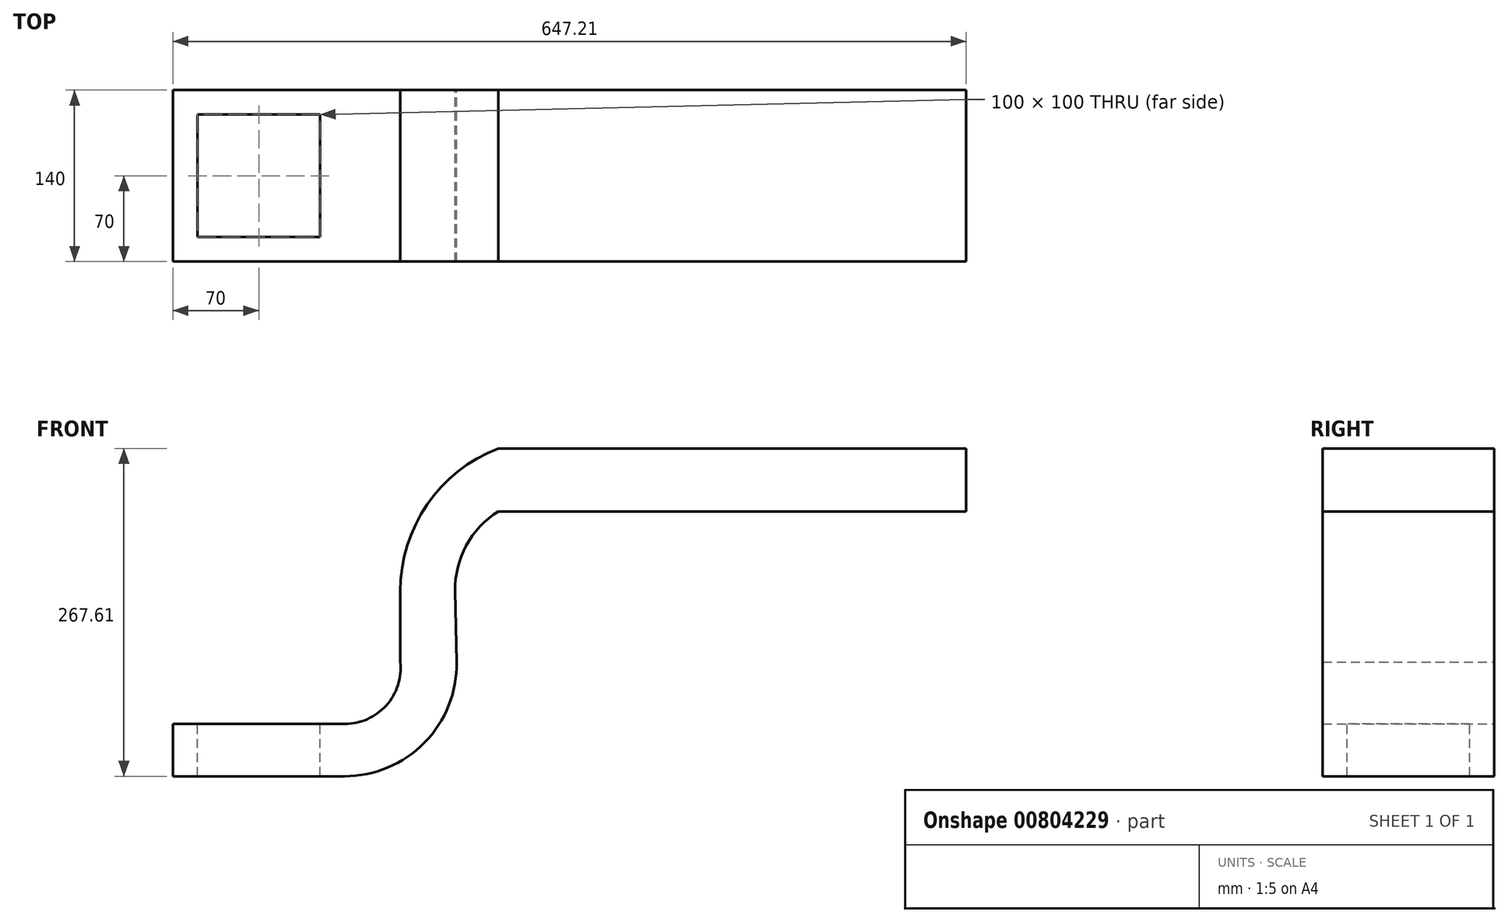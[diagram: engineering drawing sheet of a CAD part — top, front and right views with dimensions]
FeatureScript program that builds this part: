
annotation { "Feature Type Name" : "Feature", "Feature Type Description" : "" }
export const myFeature = defineFeature(function(context is Context, id is Id, definition is map)
    precondition{}
    {
        {
            var Q0;
            Q0=qCreatedBy(makeId("Front.planeOp"),FACE);
            var sketch = newSketch(context, id + "F0", { "sketchPlane" : qUnion([Q0])});
            skLineSegment(sketch, "E0", {"start": v(-140, 42.69) * mm, "end": v(-140, 0) * mm});
            skLineSegment(sketch, "E1", {"start": v(-140, 0) * mm, "end": v(0, 0) * mm});
            skArc(sketch, "E2", {"start": v(0, 0) * mm, "mid": v(65.24, 27.4) * mm, "end": v(91.34, 93.18) * mm});
            skLineSegment(sketch, "E3", {"start": v(-140, 42.69) * mm, "end": v(0, 42.69) * mm});
            skArc(sketch, "E4", {"start": v(0, 42.69) * mm, "mid": v(33.96, 57.82) * mm, "end": v(45.44, 93.18) * mm});
            skLineSegment(sketch, "E5", {"start": v(45.44, 93.18) * mm, "end": v(45.44, 151.02) * mm});
            skLineSegment(sketch, "E6", {"start": v(91.34, 93.18) * mm, "end": v(90.2, 150.92) * mm});
            skArc(sketch, "E7", {"start": v(125.31, 216.2) * mm, "mid": v(99.19, 188.17) * mm, "end": v(90.2, 150.92) * mm});
            skArc(sketch, "E8", {"start": v(125.31, 267.6) * mm, "mid": v(67.32, 221.68) * mm, "end": v(45.44, 151.02) * mm});
            skLineSegment(sketch, "E9", {"start": v(125.31, 216.2) * mm, "end": v(507.21, 216.2) * mm});
            skLineSegment(sketch, "E10", {"start": v(125.31, 267.6) * mm, "end": v(507.21, 267.6) * mm});
            skLineSegment(sketch, "E11", {"start": v(507.21, 267.6) * mm, "end": v(507.21, 216.2) * mm});
            skSolve(sketch);
        }
        {
            var Q0;
            Q0 = qSketchRegion(id + "F0", true);
            extrude(context, id + "F1", {"entities" : qUnion([Q0]), "depth" : 140 * mm, "offsetDistance" : 25.4 * mm});
        }
        {
            var Q0;
            Q0=makeQuery(id+"F1.opExtrude","SWEPT_FACE",FACE,{"disambiguationData":[OSD([sQuery(id+"F0.wireOp",EDGE,"E3")])]});
            var sketch = newSketch(context, id + "F2", { "sketchPlane" : qUnion([Q0])});
            skLineSegment(sketch, "E12.bottom", {"start": v(-20, -20) * mm, "end": v(-120, -20) * mm});
            skLineSegment(sketch, "E12.top", {"start": v(-20, -120) * mm, "end": v(-120, -120) * mm});
            skLineSegment(sketch, "E12.left", {"start": v(-20, -20) * mm, "end": v(-20, -120) * mm});
            skLineSegment(sketch, "E12.right", {"start": v(-120, -20) * mm, "end": v(-120, -120) * mm});
            skSolve(sketch);
        }
        {
            var Q0;
            Q0 = qSketchRegion(id + "F2", true);
            extrude(context, id + "F3", {"entities" : qUnion([Q0]), "operationType" : NewBodyOperationType.REMOVE, "endBound" : BoundingType.UP_TO_NEXT, "oppositeDirection" : true, "depth" : 25.4 * mm, "offsetDistance" : 25.4 * mm});
        }
    });
